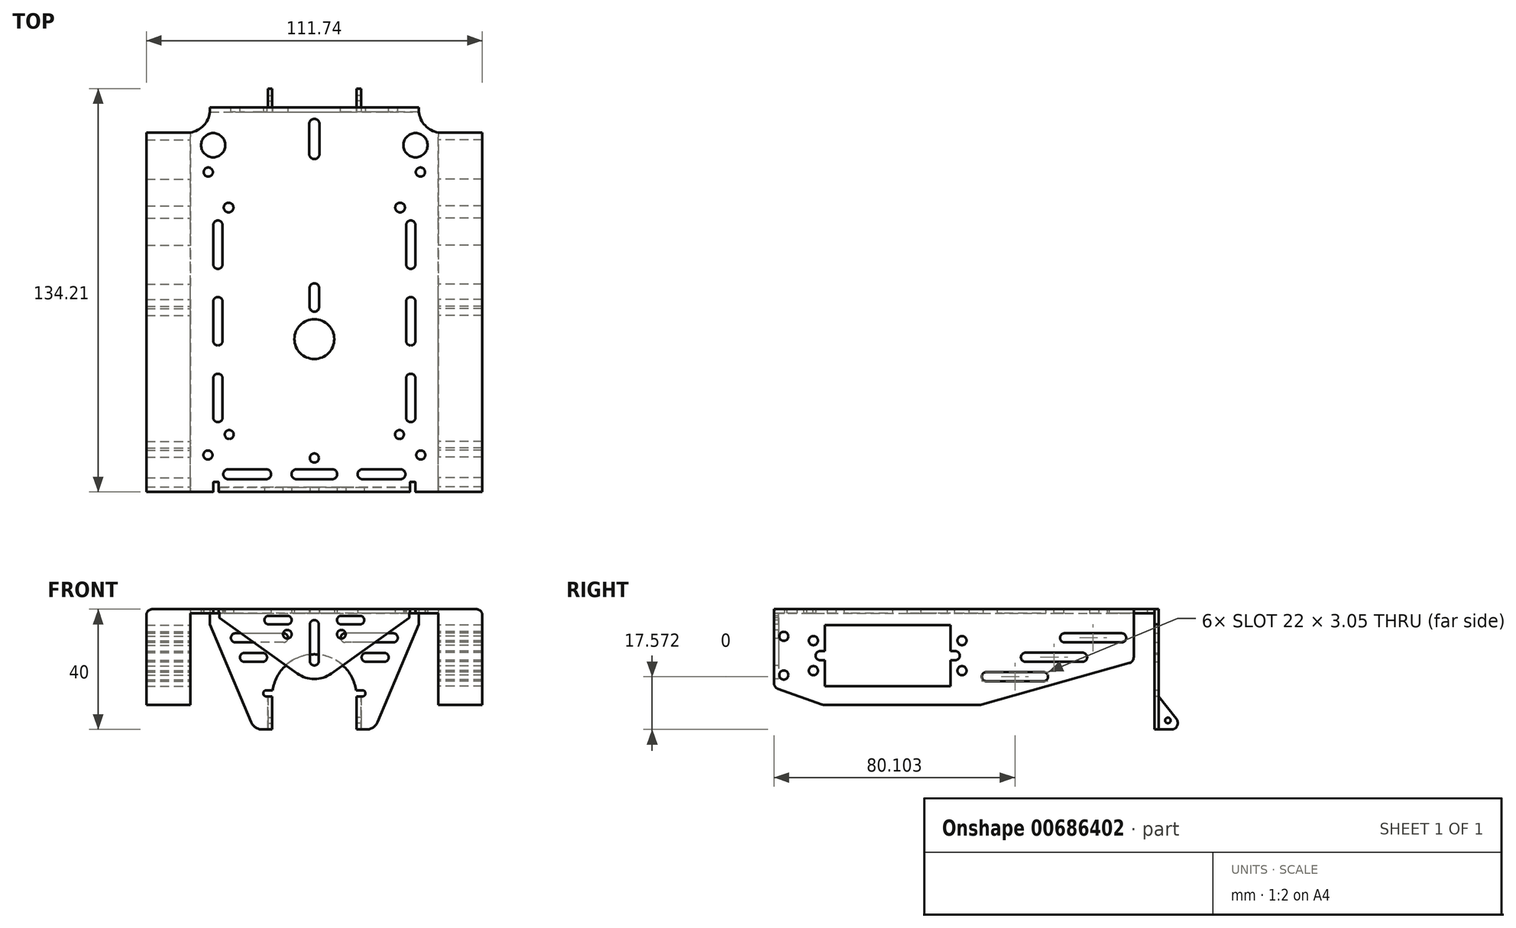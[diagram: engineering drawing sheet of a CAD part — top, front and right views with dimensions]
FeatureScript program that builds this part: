
annotation { "Feature Type Name" : "Feature", "Feature Type Description" : "" }
export const myFeature = defineFeature(function(context is Context, id is Id, definition is map)
    precondition{}
    {
        {
            var Q0;
            Q0=qCreatedBy(makeId("Top.planeOp"),FACE);
            var sketch = newSketch(context, id + "F0", { "sketchPlane" : qUnion([Q0])});
            skLineSegment(sketch, "E0", {"start": v(40.6, 10) * mm, "end": v(40.6, 161.38) * mm});
            skArc(sketch, "E1", {"start": v(40.6, 161.38) * mm, "mid": v(46.2, 164.32) * mm, "end": v(48.85, 170.09) * mm});
            skLineSegment(sketch, "E2", {"start": v(48.85, 170.09) * mm, "end": v(92.83, 170.09) * mm});
            skLineSegment(sketch, "E3", {"start": v(92.83, 170.09) * mm, "end": v(92.83, 10) * mm});
            skLineSegment(sketch, "E4", {"start": v(92.83, 10) * mm, "end": v(52.83, 10) * mm});
            skCircle(sketch, "E5", {"center": v(50.26, 156.03) * mm, "radius": 5.1 * mm});
            skCircle(sketch, "E6", {"center": v(48.18, 144.7) * mm, "radius": 1.93 * mm});
            skCircle(sketch, "E7", {"center": v(56.74, 129.77) * mm, "radius": 2.04 * mm});
            skCircle(sketch, "E8", {"center": v(57.01, 34.19) * mm, "radius": 1.88 * mm});
            skLineSegment(sketch, "E9.left", {"start": v(50.29, 122.36) * mm, "end": v(50.29, 105.92) * mm});
            skLineSegment(sketch, "E9.right", {"start": v(54.22, 122.36) * mm, "end": v(54.22, 105.92) * mm});
            skLineSegment(sketch, "E10.bottom", {"start": v(56.62, 19.58) * mm, "end": v(72.52, 19.58) * mm});
            skLineSegment(sketch, "E10.top", {"start": v(56.62, 15.38) * mm, "end": v(72.52, 15.38) * mm});
            skArc(sketch, "E11", {"start": v(50.29, 105.92) * mm, "mid": v(52.25, 103.95) * mm, "end": v(54.22, 105.92) * mm});
            skArc(sketch, "E12", {"start": v(54.22, 122.36) * mm, "mid": v(52.25, 124.33) * mm, "end": v(50.29, 122.36) * mm});
            skArc(sketch, "E13", {"start": v(56.62, 19.58) * mm, "mid": v(54.52, 17.48) * mm, "end": v(56.62, 15.38) * mm});
            skArc(sketch, "E14", {"start": v(72.52, 15.38) * mm, "mid": v(74.62, 17.48) * mm, "end": v(72.52, 19.58) * mm});
            skLineSegment(sketch, "E15.0.1.0", {"start": v(50.29, 90.1) * mm, "end": v(50.29, 73.66) * mm});
            skArc(sketch, "E15.0.1.1", {"start": v(54.22, 90.1) * mm, "mid": v(52.25, 92.07) * mm, "end": v(50.29, 90.1) * mm});
            skLineSegment(sketch, "E15.0.1.2", {"start": v(54.22, 90.1) * mm, "end": v(54.22, 73.66) * mm});
            skArc(sketch, "E15.0.1.3", {"start": v(50.29, 73.66) * mm, "mid": v(52.25, 71.7) * mm, "end": v(54.22, 73.66) * mm});
            skLineSegment(sketch, "E15.0.2.0", {"start": v(50.29, 57.84) * mm, "end": v(50.29, 41.4) * mm});
            skArc(sketch, "E15.0.2.1", {"start": v(54.22, 57.84) * mm, "mid": v(52.25, 59.8) * mm, "end": v(50.29, 57.84) * mm});
            skLineSegment(sketch, "E15.0.2.2", {"start": v(54.22, 57.84) * mm, "end": v(54.22, 41.4) * mm});
            skArc(sketch, "E15.0.2.3", {"start": v(50.29, 41.4) * mm, "mid": v(52.25, 39.43) * mm, "end": v(54.22, 41.4) * mm});
            skLineSegment(sketch, "E15.direction1", {"start": v(50.29, 105.92) * mm, "end": v(75.69, 105.92) * mm, "construction": true});
            skLineSegment(sketch, "E15.direction2", {"start": v(50.29, 105.92) * mm, "end": v(50.29, 73.66) * mm, "construction": true});
            skCircle(sketch, "E16", {"center": v(48.04, 25.57) * mm, "radius": 1.9 * mm});
            skArc(sketch, "E17", {"start": v(92.83, 82.78) * mm, "mid": v(84.45, 74.4) * mm, "end": v(92.83, 66.02) * mm});
            skArc(sketch, "E18", {"start": v(92.83, 26.24) * mm, "mid": v(90.9, 24.3) * mm, "end": v(92.83, 22.37) * mm});
            skLineSegment(sketch, "E19.left", {"start": v(90.68, 164.98) * mm, "end": v(90.68, 152.35) * mm});
            skArc(sketch, "E20", {"start": v(92.83, 167.14) * mm, "mid": v(91.3, 166.5) * mm, "end": v(90.68, 164.98) * mm});
            skArc(sketch, "E21", {"start": v(90.68, 152.35) * mm, "mid": v(91.3, 150.83) * mm, "end": v(92.83, 150.2) * mm});
            skLineSegment(sketch, "E22.left", {"start": v(90.82, 95.9) * mm, "end": v(90.82, 87.93) * mm});
            skArc(sketch, "E23", {"start": v(92.83, 97.9) * mm, "mid": v(91.4, 97.31) * mm, "end": v(90.82, 95.9) * mm});
            skArc(sketch, "E24", {"start": v(90.82, 87.93) * mm, "mid": v(91.4, 86.5) * mm, "end": v(92.83, 85.92) * mm});
            skLineSegment(sketch, "E25.1.0.0", {"start": v(85.32, 19.58) * mm, "end": v(92.83, 19.58) * mm});
            skArc(sketch, "E25.1.0.1", {"start": v(85.32, 19.58) * mm, "mid": v(83.22, 17.48) * mm, "end": v(85.32, 15.38) * mm});
            skLineSegment(sketch, "E25.1.0.2", {"start": v(85.32, 15.38) * mm, "end": v(92.83, 15.38) * mm});
            skLineSegment(sketch, "E25.direction1", {"start": v(56.62, 15.38) * mm, "end": v(85.32, 15.38) * mm, "construction": true});
            skPoint(sketch, "E26.orphan", {"position": v(101.22, 15.38) * mm});
            skArc(sketch, "E27.MirrorCS", {"start": v(135.38, 105.92) * mm, "mid": v(133.4, 103.95) * mm, "end": v(131.44, 105.92) * mm});
            skArc(sketch, "E28.MirrorCS", {"start": v(131.44, 90.1) * mm, "mid": v(133.4, 92.07) * mm, "end": v(135.38, 90.1) * mm});
            skArc(sketch, "E29.MirrorCS", {"start": v(100.34, 19.58) * mm, "mid": v(102.44, 17.48) * mm, "end": v(100.34, 15.38) * mm});
            skArc(sketch, "E30.MirrorCS", {"start": v(135.38, 41.4) * mm, "mid": v(133.4, 39.43) * mm, "end": v(131.44, 41.4) * mm});
            skArc(sketch, "E31.MirrorCS", {"start": v(113.14, 15.38) * mm, "mid": v(111.04, 17.48) * mm, "end": v(113.14, 19.58) * mm});
            skArc(sketch, "E32.MirrorCS", {"start": v(129.04, 19.58) * mm, "mid": v(131.14, 17.48) * mm, "end": v(129.04, 15.38) * mm});
            skArc(sketch, "E33.MirrorCS", {"start": v(94.84, 87.93) * mm, "mid": v(94.25, 86.5) * mm, "end": v(92.83, 85.92) * mm});
            skArc(sketch, "E34.MirrorCS", {"start": v(135.38, 73.66) * mm, "mid": v(133.4, 71.7) * mm, "end": v(131.44, 73.66) * mm});
            skArc(sketch, "E35.MirrorCS", {"start": v(145.06, 161.38) * mm, "mid": v(139.45, 164.32) * mm, "end": v(136.82, 170.09) * mm});
            skArc(sketch, "E36.MirrorCS", {"start": v(131.44, 57.84) * mm, "mid": v(133.4, 59.8) * mm, "end": v(135.38, 57.84) * mm});
            skArc(sketch, "E37.MirrorCS", {"start": v(131.44, 122.36) * mm, "mid": v(133.4, 124.33) * mm, "end": v(135.38, 122.36) * mm});
            skArc(sketch, "E38.MirrorCS", {"start": v(92.83, 97.9) * mm, "mid": v(94.25, 97.31) * mm, "end": v(94.84, 95.9) * mm});
            skLineSegment(sketch, "E39.MirrorCS", {"start": v(94.99, 164.98) * mm, "end": v(94.99, 152.35) * mm});
            skLineSegment(sketch, "E40.MirrorCS", {"start": v(94.84, 95.9) * mm, "end": v(94.84, 87.93) * mm});
            skLineSegment(sketch, "E41.MirrorCS", {"start": v(100.34, 19.58) * mm, "end": v(92.83, 19.58) * mm});
            skArc(sketch, "E42.MirrorCS", {"start": v(92.83, 167.14) * mm, "mid": v(94.35, 166.5) * mm, "end": v(94.99, 164.98) * mm});
            skArc(sketch, "E43.MirrorCS", {"start": v(94.99, 152.35) * mm, "mid": v(94.35, 150.83) * mm, "end": v(92.83, 150.2) * mm});
            skLineSegment(sketch, "E44.MirrorCS", {"start": v(100.34, 15.38) * mm, "end": v(92.83, 15.38) * mm});
            skArc(sketch, "E45.MirrorCS", {"start": v(92.83, 26.24) * mm, "mid": v(94.77, 24.3) * mm, "end": v(92.83, 22.37) * mm});
            skCircle(sketch, "E46.MirrorC", {"center": v(128.92, 129.77) * mm, "radius": 2.04 * mm});
            skCircle(sketch, "E47.MirrorC", {"center": v(137.62, 25.57) * mm, "radius": 1.9 * mm});
            skCircle(sketch, "E48.MirrorC", {"center": v(137.48, 144.7) * mm, "radius": 1.93 * mm});
            skCircle(sketch, "E49.MirrorC", {"center": v(128.65, 34.19) * mm, "radius": 1.88 * mm});
            skLineSegment(sketch, "E50.MirrorCS", {"start": v(129.04, 15.38) * mm, "end": v(100.34, 15.38) * mm, "construction": true});
            skPoint(sketch, "E51.MirrorP", {"position": v(84.44, 15.38) * mm});
            skCircle(sketch, "E52.MirrorC", {"center": v(135.4, 156.03) * mm, "radius": 5.1 * mm});
            skLineSegment(sketch, "E53.MirrorCS", {"start": v(135.38, 122.36) * mm, "end": v(135.38, 105.92) * mm});
            skLineSegment(sketch, "E54.MirrorCS", {"start": v(135.38, 57.84) * mm, "end": v(135.38, 41.4) * mm});
            skLineSegment(sketch, "E55.MirrorCS", {"start": v(92.83, 10) * mm, "end": v(132.84, 10) * mm});
            skLineSegment(sketch, "E56.MirrorCS", {"start": v(135.38, 105.92) * mm, "end": v(109.98, 105.92) * mm, "construction": true});
            skLineSegment(sketch, "E57.MirrorCS", {"start": v(135.38, 105.92) * mm, "end": v(135.38, 73.66) * mm, "construction": true});
            skLineSegment(sketch, "E58.MirrorCS", {"start": v(135.38, 90.1) * mm, "end": v(135.38, 73.66) * mm});
            skLineSegment(sketch, "E59.MirrorCS", {"start": v(129.04, 19.58) * mm, "end": v(113.14, 19.58) * mm});
            skLineSegment(sketch, "E60.MirrorCS", {"start": v(131.44, 57.84) * mm, "end": v(131.44, 41.4) * mm});
            skLineSegment(sketch, "E61.MirrorCS", {"start": v(129.04, 15.38) * mm, "end": v(113.14, 15.38) * mm});
            skLineSegment(sketch, "E62.MirrorCS", {"start": v(131.44, 122.36) * mm, "end": v(131.44, 105.92) * mm});
            skLineSegment(sketch, "E63.MirrorCS", {"start": v(145.06, 10) * mm, "end": v(145.06, 161.38) * mm});
            skLineSegment(sketch, "E64.MirrorCS", {"start": v(131.44, 90.1) * mm, "end": v(131.44, 73.66) * mm});
            skLineSegment(sketch, "E65.MirrorCS", {"start": v(136.82, 170.09) * mm, "end": v(92.83, 170.09) * mm});
            skArc(sketch, "E66.MirrorCS", {"start": v(92.83, 82.78) * mm, "mid": v(101.21, 74.4) * mm, "end": v(92.83, 66.02) * mm});
            skLineSegment(sketch, "E67", {"start": v(50.36, 10.25) * mm, "end": v(50.36, 14.04) * mm});
            skLineSegment(sketch, "E68", {"start": v(50.62, 14.3) * mm, "end": v(52.32, 14.3) * mm});
            skLineSegment(sketch, "E69", {"start": v(52.57, 14.04) * mm, "end": v(52.57, 10.25) * mm});
            skLineSegment(sketch, "E70.trimOffspring", {"start": v(50.1, 10) * mm, "end": v(40.6, 10) * mm});
            skPoint(sketch, "E71.visualSharp", {"position": v(50.36, 10) * mm});
            skArc(sketch, "E71.filletArc", {"start": v(50.1, 10) * mm, "mid": v(50.29, 10.07) * mm, "end": v(50.36, 10.25) * mm});
            skPoint(sketch, "E72.visualSharp", {"position": v(52.57, 10) * mm});
            skArc(sketch, "E72.filletArc", {"start": v(52.57, 10.25) * mm, "mid": v(52.65, 10.07) * mm, "end": v(52.83, 10) * mm});
            skPoint(sketch, "E73.visualSharp", {"position": v(50.36, 14.3) * mm});
            skArc(sketch, "E73.filletArc", {"start": v(50.62, 14.3) * mm, "mid": v(50.44, 14.22) * mm, "end": v(50.36, 14.04) * mm});
            skPoint(sketch, "E74.visualSharp", {"position": v(52.57, 14.3) * mm});
            skArc(sketch, "E74.filletArc", {"start": v(52.57, 14.04) * mm, "mid": v(52.5, 14.22) * mm, "end": v(52.32, 14.3) * mm});
            skArc(sketch, "E75.MirrorCS", {"start": v(133.09, 10.25) * mm, "mid": v(133.01, 10.07) * mm, "end": v(132.84, 10) * mm});
            skLineSegment(sketch, "E76.MirrorCS", {"start": v(133.09, 14.04) * mm, "end": v(133.09, 10.25) * mm});
            skArc(sketch, "E77.MirrorCS", {"start": v(133.09, 14.04) * mm, "mid": v(133.16, 14.22) * mm, "end": v(133.34, 14.3) * mm});
            skLineSegment(sketch, "E78.MirrorCS", {"start": v(135.3, 10.25) * mm, "end": v(135.3, 14.04) * mm});
            skLineSegment(sketch, "E79.MirrorCS", {"start": v(135.05, 14.3) * mm, "end": v(133.34, 14.3) * mm});
            skArc(sketch, "E80.MirrorCS", {"start": v(135.05, 14.3) * mm, "mid": v(135.23, 14.22) * mm, "end": v(135.3, 14.04) * mm});
            skArc(sketch, "E81.MirrorCS", {"start": v(135.55, 10) * mm, "mid": v(135.37, 10.07) * mm, "end": v(135.3, 10.25) * mm});
            skLineSegment(sketch, "E82.trimOffspring", {"start": v(135.55, 10) * mm, "end": v(145.06, 10) * mm});
            skSolve(sketch);
        }
        {
            var Q0;
            Q0 = qSketchRegion(id + "F0", true);
            extrude(context, id + "F1", {"entities" : qUnion([Q0]), "depth" : 1.65 * mm, "offsetDistance" : 25.4 * mm});
        }
        {
            var Q0;
            Q0=makeQuery(id+"F1.opExtrude","SWEPT_BODY",BODY,{"disambiguationData":[OSD([sQuery(id+"F0.wireOp",EDGE,"E0"),sQuery(id+"F0.wireOp",EDGE,"E1"),sQuery(id+"F0.wireOp",EDGE,"E2"),sQuery(id+"F0.wireOp",EDGE,"E4"),sQuery(id+"F0.wireOp",EDGE,"E5"),sQuery(id+"F0.wireOp",EDGE,"E6"),sQuery(id+"F0.wireOp",EDGE,"E7"),sQuery(id+"F0.wireOp",EDGE,"E8"),sQuery(id+"F0.wireOp",EDGE,"E9.left"),sQuery(id+"F0.wireOp",EDGE,"E9.right"),sQuery(id+"F0.wireOp",EDGE,"E10.bottom"),sQuery(id+"F0.wireOp",EDGE,"E10.top"),sQuery(id+"F0.wireOp",EDGE,"E11"),sQuery(id+"F0.wireOp",EDGE,"E12"),sQuery(id+"F0.wireOp",EDGE,"E13"),sQuery(id+"F0.wireOp",EDGE,"E14"),sQuery(id+"F0.wireOp",EDGE,"E15.0.1.0"),sQuery(id+"F0.wireOp",EDGE,"E15.0.1.1"),sQuery(id+"F0.wireOp",EDGE,"E15.0.1.2"),sQuery(id+"F0.wireOp",EDGE,"E15.0.1.3"),sQuery(id+"F0.wireOp",EDGE,"E15.0.2.0"),sQuery(id+"F0.wireOp",EDGE,"E15.0.2.1"),sQuery(id+"F0.wireOp",EDGE,"E15.0.2.2"),sQuery(id+"F0.wireOp",EDGE,"E15.0.2.3"),sQuery(id+"F0.wireOp",EDGE,"E16"),sQuery(id+"F0.wireOp",EDGE,"E17"),sQuery(id+"F0.wireOp",EDGE,"E18"),sQuery(id+"F0.wireOp",EDGE,"E19.left"),sQuery(id+"F0.wireOp",EDGE,"E20"),sQuery(id+"F0.wireOp",EDGE,"E21"),sQuery(id+"F0.wireOp",EDGE,"E22.left"),sQuery(id+"F0.wireOp",EDGE,"E23"),sQuery(id+"F0.wireOp",EDGE,"E24"),sQuery(id+"F0.wireOp",EDGE,"E25.1.0.0"),sQuery(id+"F0.wireOp",EDGE,"E25.1.0.1"),sQuery(id+"F0.wireOp",EDGE,"E25.1.0.2"),sQuery(id+"F0.wireOp",EDGE,"E27.MirrorCS"),sQuery(id+"F0.wireOp",EDGE,"E28.MirrorCS"),sQuery(id+"F0.wireOp",EDGE,"E29.MirrorCS"),sQuery(id+"F0.wireOp",EDGE,"E30.MirrorCS"),sQuery(id+"F0.wireOp",EDGE,"E31.MirrorCS"),sQuery(id+"F0.wireOp",EDGE,"E32.MirrorCS"),sQuery(id+"F0.wireOp",EDGE,"E33.MirrorCS"),sQuery(id+"F0.wireOp",EDGE,"E34.MirrorCS"),sQuery(id+"F0.wireOp",EDGE,"E35.MirrorCS"),sQuery(id+"F0.wireOp",EDGE,"E36.MirrorCS"),sQuery(id+"F0.wireOp",EDGE,"E37.MirrorCS"),sQuery(id+"F0.wireOp",EDGE,"E38.MirrorCS"),sQuery(id+"F0.wireOp",EDGE,"E39.MirrorCS"),sQuery(id+"F0.wireOp",EDGE,"E40.MirrorCS"),sQuery(id+"F0.wireOp",EDGE,"E41.MirrorCS"),sQuery(id+"F0.wireOp",EDGE,"E42.MirrorCS"),sQuery(id+"F0.wireOp",EDGE,"E43.MirrorCS"),sQuery(id+"F0.wireOp",EDGE,"E44.MirrorCS"),sQuery(id+"F0.wireOp",EDGE,"E45.MirrorCS"),sQuery(id+"F0.wireOp",EDGE,"E46.MirrorC"),sQuery(id+"F0.wireOp",EDGE,"E47.MirrorC"),sQuery(id+"F0.wireOp",EDGE,"E48.MirrorC"),sQuery(id+"F0.wireOp",EDGE,"E49.MirrorC"),sQuery(id+"F0.wireOp",EDGE,"E52.MirrorC"),sQuery(id+"F0.wireOp",EDGE,"E53.MirrorCS"),sQuery(id+"F0.wireOp",EDGE,"E54.MirrorCS"),sQuery(id+"F0.wireOp",EDGE,"E55.MirrorCS"),sQuery(id+"F0.wireOp",EDGE,"E58.MirrorCS"),sQuery(id+"F0.wireOp",EDGE,"E59.MirrorCS"),sQuery(id+"F0.wireOp",EDGE,"E60.MirrorCS"),sQuery(id+"F0.wireOp",EDGE,"E61.MirrorCS"),sQuery(id+"F0.wireOp",EDGE,"E62.MirrorCS"),sQuery(id+"F0.wireOp",EDGE,"E63.MirrorCS"),sQuery(id+"F0.wireOp",EDGE,"E64.MirrorCS"),sQuery(id+"F0.wireOp",EDGE,"E65.MirrorCS"),sQuery(id+"F0.wireOp",EDGE,"E66.MirrorCS")])]});
            var Q1;
            Q1=qCreatedBy(makeId("Origin.pointOp"),VERTEX);
            transform(context, id + "F2", {"entities" : qUnion([Q0]), "transformType" : TransformType.SCALE_UNIFORMLY, "scale" : .83151, "scalePoint" : qUnion([Q1]), "makeCopy" : false});
        }
        {
            var Q0;
            Q0=makeQuery(id+"F1.opExtrude","SWEPT_FACE",FACE,{"disambiguationData":[OSD([sQuery(id+"F0.wireOp",EDGE,"E4")])]});
            var sketch = newSketch(context, id + "F3", { "sketchPlane" : qUnion([Q0])});
            skLineSegment(sketch, "E83", {"start": v(43.93, -1.68) * mm, "end": v(43.93, 0) * mm});
            skLineSegment(sketch, "E84", {"start": v(110.45, 0) * mm, "end": v(110.45, -1.68) * mm});
            skLineSegment(sketch, "E85", {"start": v(43.93, 0) * mm, "end": v(110.45, 0) * mm});
            skLineSegment(sketch, "E86", {"start": v(43.93, -1.68) * mm, "end": v(71.3, -21.2) * mm});
            skLineSegment(sketch, "E87", {"start": v(83.09, -21.2) * mm, "end": v(110.45, -1.68) * mm});
            skLineSegment(sketch, "E88", {"start": v(77.19, -25.4) * mm, "end": v(77.19, 0) * mm, "construction": true});
            skPoint(sketch, "E89.visualSharp", {"position": v(77.19, -25.4) * mm});
            skArc(sketch, "E89.filletArc", {"start": v(71.3, -21.2) * mm, "mid": v(77.19, -23.08) * mm, "end": v(83.09, -21.2) * mm});
            skPoint(sketch, "E90", {"position": v(77.19, -23.08) * mm});
            skArc(sketch, "E91", {"start": v(78.74, -3.99) * mm, "mid": v(77.19, -2.44) * mm, "end": v(75.64, -3.99) * mm});
            skLineSegment(sketch, "E92", {"start": v(75.64, -3.99) * mm, "end": v(75.64, -10.37) * mm});
            skLineSegment(sketch, "E93", {"start": v(78.74, -3.99) * mm, "end": v(78.74, -10.37) * mm});
            skPoint(sketch, "E94", {"position": v(77.19, -2.44) * mm});
            skLineSegment(sketch, "E95", {"start": v(75.64, -10.37) * mm, "end": v(78.74, -10.37) * mm, "construction": true});
            skLineSegment(sketch, "E96.MirrorCS", {"start": v(78.74, -16.76) * mm, "end": v(78.74, -10.37) * mm});
            skLineSegment(sketch, "E97.MirrorCS", {"start": v(75.64, -16.76) * mm, "end": v(75.64, -10.37) * mm});
            skArc(sketch, "E98.MirrorCS", {"start": v(78.74, -16.76) * mm, "mid": v(77.19, -18.31) * mm, "end": v(75.64, -16.76) * mm});
            skArc(sketch, "E99", {"start": v(86.65, -0.91) * mm, "mid": v(85.13, -2.44) * mm, "end": v(86.65, -3.96) * mm});
            skLineSegment(sketch, "E100", {"start": v(86.65, -0.91) * mm, "end": v(89.89, -0.91) * mm});
            skLineSegment(sketch, "E101", {"start": v(86.65, -3.96) * mm, "end": v(89.89, -3.96) * mm});
            skLineSegment(sketch, "E102", {"start": v(86.65, -2.44) * mm, "end": v(85.13, -2.44) * mm, "construction": true});
            skPoint(sketch, "E103", {"position": v(85.13, -2.44) * mm});
            skLineSegment(sketch, "E104", {"start": v(89.89, -0.91) * mm, "end": v(89.89, -3.96) * mm, "construction": true});
            skLineSegment(sketch, "E105.MirrorCS", {"start": v(93.13, -0.91) * mm, "end": v(89.89, -0.91) * mm});
            skLineSegment(sketch, "E106.MirrorCS", {"start": v(93.13, -3.96) * mm, "end": v(89.89, -3.96) * mm});
            skArc(sketch, "E107.MirrorCS", {"start": v(93.13, -0.91) * mm, "mid": v(94.65, -2.44) * mm, "end": v(93.13, -3.96) * mm});
            skLineSegment(sketch, "E108.MirrorCS", {"start": v(67.73, -2.44) * mm, "end": v(69.25, -2.44) * mm, "construction": true});
            skLineSegment(sketch, "E109.MirrorCS", {"start": v(64.49, -0.91) * mm, "end": v(64.49, -3.96) * mm, "construction": true});
            skLineSegment(sketch, "E110.MirrorCS", {"start": v(67.73, -3.96) * mm, "end": v(64.49, -3.96) * mm});
            skLineSegment(sketch, "E111.MirrorCS", {"start": v(67.73, -0.91) * mm, "end": v(64.49, -0.91) * mm});
            skLineSegment(sketch, "E112.MirrorCS", {"start": v(61.25, -3.96) * mm, "end": v(64.49, -3.96) * mm});
            skArc(sketch, "E113.MirrorCS", {"start": v(67.73, -0.91) * mm, "mid": v(69.25, -2.44) * mm, "end": v(67.73, -3.96) * mm});
            skLineSegment(sketch, "E114.MirrorCS", {"start": v(61.25, -0.91) * mm, "end": v(64.49, -0.91) * mm});
            skArc(sketch, "E115.MirrorCS", {"start": v(61.25, -0.91) * mm, "mid": v(59.73, -2.44) * mm, "end": v(61.25, -3.96) * mm});
            skPoint(sketch, "E116.MirrorP", {"position": v(69.25, -2.44) * mm});
            skCircle(sketch, "E117", {"center": v(86.65, -7.4) * mm, "radius": 1.52 * mm});
            skCircle(sketch, "E118.MirrorC", {"center": v(67.73, -7.4) * mm, "radius": 1.52 * mm});
            skSolve(sketch);
        }
        {
            var Q0;
            Q0 = qSketchRegion(id + "F3", true);
            extrude(context, id + "F4", {"entities" : qUnion([Q0]), "operationType" : NewBodyOperationType.ADD, "oppositeDirection" : true, "depth" : 1.65 * mm, "offsetDistance" : 25.4 * mm});
        }
        {
            var Q0;
            Q0=makeQuery(id+"F1.opExtrude","CAP_EDGE",EDGE,{"disambiguationData":[OSD([sQuery(id+"F0.wireOp",EDGE,"E4"),sQuery(id+"F0.wireOp",EDGE,"E55.MirrorCS")])],"isStart":false});
            fillet(context, id + "F5", {"entities" : qUnion([Q0]), "radius" : 1.27 * mm, "allowEdgeOverflow" : false});
        }
        {
            var Q0;
            Q0=makeQuery(id+"F1.opExtrude","SWEPT_BODY",BODY,{"disambiguationData":[OSD([sQuery(id+"F0.wireOp",EDGE,"E0"),sQuery(id+"F0.wireOp",EDGE,"E1"),sQuery(id+"F0.wireOp",EDGE,"E2"),sQuery(id+"F0.wireOp",EDGE,"E4"),sQuery(id+"F0.wireOp",EDGE,"E5"),sQuery(id+"F0.wireOp",EDGE,"E6"),sQuery(id+"F0.wireOp",EDGE,"E7"),sQuery(id+"F0.wireOp",EDGE,"E8"),sQuery(id+"F0.wireOp",EDGE,"E9.left"),sQuery(id+"F0.wireOp",EDGE,"E9.right"),sQuery(id+"F0.wireOp",EDGE,"E10.bottom"),sQuery(id+"F0.wireOp",EDGE,"E10.top"),sQuery(id+"F0.wireOp",EDGE,"E11"),sQuery(id+"F0.wireOp",EDGE,"E12"),sQuery(id+"F0.wireOp",EDGE,"E13"),sQuery(id+"F0.wireOp",EDGE,"E14"),sQuery(id+"F0.wireOp",EDGE,"E15.0.1.0"),sQuery(id+"F0.wireOp",EDGE,"E15.0.1.1"),sQuery(id+"F0.wireOp",EDGE,"E15.0.1.2"),sQuery(id+"F0.wireOp",EDGE,"E15.0.1.3"),sQuery(id+"F0.wireOp",EDGE,"E15.0.2.0"),sQuery(id+"F0.wireOp",EDGE,"E15.0.2.1"),sQuery(id+"F0.wireOp",EDGE,"E15.0.2.2"),sQuery(id+"F0.wireOp",EDGE,"E15.0.2.3"),sQuery(id+"F0.wireOp",EDGE,"E16"),sQuery(id+"F0.wireOp",EDGE,"E17"),sQuery(id+"F0.wireOp",EDGE,"E18"),sQuery(id+"F0.wireOp",EDGE,"E19.left"),sQuery(id+"F0.wireOp",EDGE,"E20"),sQuery(id+"F0.wireOp",EDGE,"E21"),sQuery(id+"F0.wireOp",EDGE,"E22.left"),sQuery(id+"F0.wireOp",EDGE,"E23"),sQuery(id+"F0.wireOp",EDGE,"E24"),sQuery(id+"F0.wireOp",EDGE,"E25.1.0.0"),sQuery(id+"F0.wireOp",EDGE,"E25.1.0.1"),sQuery(id+"F0.wireOp",EDGE,"E25.1.0.2"),sQuery(id+"F0.wireOp",EDGE,"E27.MirrorCS"),sQuery(id+"F0.wireOp",EDGE,"E28.MirrorCS"),sQuery(id+"F0.wireOp",EDGE,"E29.MirrorCS"),sQuery(id+"F0.wireOp",EDGE,"E30.MirrorCS"),sQuery(id+"F0.wireOp",EDGE,"E31.MirrorCS"),sQuery(id+"F0.wireOp",EDGE,"E32.MirrorCS"),sQuery(id+"F0.wireOp",EDGE,"E33.MirrorCS"),sQuery(id+"F0.wireOp",EDGE,"E34.MirrorCS"),sQuery(id+"F0.wireOp",EDGE,"E35.MirrorCS"),sQuery(id+"F0.wireOp",EDGE,"E36.MirrorCS"),sQuery(id+"F0.wireOp",EDGE,"E37.MirrorCS"),sQuery(id+"F0.wireOp",EDGE,"E38.MirrorCS"),sQuery(id+"F0.wireOp",EDGE,"E39.MirrorCS"),sQuery(id+"F0.wireOp",EDGE,"E40.MirrorCS"),sQuery(id+"F0.wireOp",EDGE,"E41.MirrorCS"),sQuery(id+"F0.wireOp",EDGE,"E42.MirrorCS"),sQuery(id+"F0.wireOp",EDGE,"E43.MirrorCS"),sQuery(id+"F0.wireOp",EDGE,"E44.MirrorCS"),sQuery(id+"F0.wireOp",EDGE,"E45.MirrorCS"),sQuery(id+"F0.wireOp",EDGE,"E46.MirrorC"),sQuery(id+"F0.wireOp",EDGE,"E47.MirrorC"),sQuery(id+"F0.wireOp",EDGE,"E48.MirrorC"),sQuery(id+"F0.wireOp",EDGE,"E49.MirrorC"),sQuery(id+"F0.wireOp",EDGE,"E52.MirrorC"),sQuery(id+"F0.wireOp",EDGE,"E53.MirrorCS"),sQuery(id+"F0.wireOp",EDGE,"E54.MirrorCS"),sQuery(id+"F0.wireOp",EDGE,"E55.MirrorCS"),sQuery(id+"F0.wireOp",EDGE,"E58.MirrorCS"),sQuery(id+"F0.wireOp",EDGE,"E59.MirrorCS"),sQuery(id+"F0.wireOp",EDGE,"E60.MirrorCS"),sQuery(id+"F0.wireOp",EDGE,"E61.MirrorCS"),sQuery(id+"F0.wireOp",EDGE,"E62.MirrorCS"),sQuery(id+"F0.wireOp",EDGE,"E63.MirrorCS"),sQuery(id+"F0.wireOp",EDGE,"E64.MirrorCS"),sQuery(id+"F0.wireOp",EDGE,"E65.MirrorCS"),sQuery(id+"F0.wireOp",EDGE,"E66.MirrorCS"),sQuery(id+"F0.wireOp",EDGE,"E67"),sQuery(id+"F0.wireOp",EDGE,"E68"),sQuery(id+"F0.wireOp",EDGE,"E69"),sQuery(id+"F0.wireOp",EDGE,"E70.trimOffspring"),sQuery(id+"F0.wireOp",EDGE,"E71.filletArc"),sQuery(id+"F0.wireOp",EDGE,"E72.filletArc"),sQuery(id+"F0.wireOp",EDGE,"E73.filletArc"),sQuery(id+"F0.wireOp",EDGE,"E74.filletArc"),sQuery(id+"F0.wireOp",EDGE,"E75.MirrorCS"),sQuery(id+"F0.wireOp",EDGE,"E76.MirrorCS"),sQuery(id+"F0.wireOp",EDGE,"E77.MirrorCS"),sQuery(id+"F0.wireOp",EDGE,"E78.MirrorCS"),sQuery(id+"F0.wireOp",EDGE,"E79.MirrorCS"),sQuery(id+"F0.wireOp",EDGE,"E80.MirrorCS"),sQuery(id+"F0.wireOp",EDGE,"E81.MirrorCS"),sQuery(id+"F0.wireOp",EDGE,"E82.trimOffspring")])]});
            var Q1;
            Q1=qCreatedBy(makeId("Origin.pointOp"),VERTEX);
            transform(context, id + "F6", {"entities" : qUnion([Q0]), "transformType" : TransformType.SCALE_UNIFORMLY, "scale" : .95, "scalePoint" : qUnion([Q1]), "makeCopy" : false});
        }
        {
            var Q0;
            Q0=makeQuery(id+"F1.opExtrude","SWEPT_FACE",FACE,{"disambiguationData":[OSD([sQuery(id+"F0.wireOp",EDGE,"E0")])]});
            var sketch = newSketch(context, id + "F7", { "sketchPlane" : qUnion([Q0])});
            skLineSegment(sketch, "E119", {"start": v(-7.9, 1.3) * mm, "end": v(-7.9, -23.29) * mm});
            skLineSegment(sketch, "E120", {"start": v(-9.22, -25.17) * mm, "end": v(-23.83, -30.38) * mm});
            skLineSegment(sketch, "E121", {"start": v(-24.5, -30.5) * mm, "end": v(-76.4, -30.5) * mm});
            skLineSegment(sketch, "E122", {"start": v(-76.94, -30.42) * mm, "end": v(-126.02, -16.6) * mm});
            skLineSegment(sketch, "E123", {"start": v(-127.48, -14.68) * mm, "end": v(-127.48, 1.3) * mm});
            skPoint(sketch, "E124.visualSharp", {"position": v(-127.48, -16.2) * mm});
            skArc(sketch, "E124.filletArc", {"start": v(-127.48, -14.68) * mm, "mid": v(-127.07, -15.89) * mm, "end": v(-126.02, -16.6) * mm});
            skPoint(sketch, "E125.visualSharp", {"position": v(-76.68, -30.5) * mm});
            skArc(sketch, "E125.filletArc", {"start": v(-76.94, -30.42) * mm, "mid": v(-76.67, -30.48) * mm, "end": v(-76.4, -30.5) * mm});
            skPoint(sketch, "E126.visualSharp", {"position": v(-24.15, -30.5) * mm});
            skArc(sketch, "E126.filletArc", {"start": v(-24.5, -30.5) * mm, "mid": v(-24.16, -30.47) * mm, "end": v(-23.83, -30.38) * mm});
            skPoint(sketch, "E127.visualSharp", {"position": v(-7.9, -24.7) * mm});
            skArc(sketch, "E127.filletArc", {"start": v(-9.22, -25.17) * mm, "mid": v(-8.26, -24.44) * mm, "end": v(-7.9, -23.29) * mm});
            skLineSegment(sketch, "E128", {"start": v(-127.48, 1.3) * mm, "end": v(-7.9, 1.3) * mm});
            skLineSegment(sketch, "E129.bottom", {"start": v(-66.64, -4.02) * mm, "end": v(-24.74, -4.02) * mm});
            skLineSegment(sketch, "E129.top", {"start": v(-66.64, -24.27) * mm, "end": v(-24.74, -24.27) * mm});
            skLineSegment(sketch, "E129.left", {"start": v(-66.64, -4.02) * mm, "end": v(-66.64, -12.64) * mm});
            skLineSegment(sketch, "E129.right", {"start": v(-24.74, -4.02) * mm, "end": v(-24.74, -12.64) * mm});
            skLineSegment(sketch, "E130", {"start": v(-45.7, -4.02) * mm, "end": v(-45.7, -24.27) * mm, "construction": true});
            skArc(sketch, "E131", {"start": v(-68.14, -12.64) * mm, "mid": v(-69.64, -14.14) * mm, "end": v(-68.14, -15.64) * mm});
            skPoint(sketch, "E131.centerSnap0", {"position": v(-66.64, -14.14) * mm});
            skLineSegment(sketch, "E132", {"start": v(-68.14, -12.64) * mm, "end": v(-66.64, -12.64) * mm});
            skLineSegment(sketch, "E133", {"start": v(-68.14, -15.64) * mm, "end": v(-66.64, -15.64) * mm});
            skLineSegment(sketch, "E134.trimOffspring", {"start": v(-66.64, -15.64) * mm, "end": v(-66.64, -24.27) * mm});
            skArc(sketch, "E135.MirrorCS", {"start": v(-23.24, -12.64) * mm, "mid": v(-21.74, -14.14) * mm, "end": v(-23.24, -15.64) * mm});
            skPoint(sketch, "E136.MirrorP", {"position": v(-24.74, -14.14) * mm});
            skLineSegment(sketch, "E137.MirrorCS", {"start": v(-23.24, -15.64) * mm, "end": v(-24.74, -15.64) * mm});
            skLineSegment(sketch, "E138.MirrorCS", {"start": v(-23.24, -12.64) * mm, "end": v(-24.74, -12.64) * mm});
            skLineSegment(sketch, "E139.trimOffspring", {"start": v(-24.74, -15.64) * mm, "end": v(-24.74, -24.27) * mm});
            skLineSegment(sketch, "E140", {"start": v(-68.14, -14.14) * mm, "end": v(-23.24, -14.14) * mm, "construction": true});
            skCircle(sketch, "E141", {"center": v(-70.4, -9.14) * mm, "radius": 1.52 * mm});
            skCircle(sketch, "E142.0.1.0", {"center": v(-70.4, -19.14) * mm, "radius": 1.52 * mm});
            skCircle(sketch, "E142.1.0.0", {"center": v(-21, -9.14) * mm, "radius": 1.52 * mm});
            skCircle(sketch, "E142.1.1.0", {"center": v(-21, -19.14) * mm, "radius": 1.52 * mm});
            skLineSegment(sketch, "E142.direction1", {"start": v(-70.4, -9.14) * mm, "end": v(-21, -9.14) * mm, "construction": true});
            skLineSegment(sketch, "E142.direction2", {"start": v(-70.4, -9.14) * mm, "end": v(-70.4, -19.14) * mm, "construction": true});
            skCircle(sketch, "E143", {"center": v(-11.15, -7.72) * mm, "radius": 1.52 * mm});
            skCircle(sketch, "E144", {"center": v(-11.15, -20.57) * mm, "radius": 1.52 * mm});
            skLineSegment(sketch, "E145", {"start": v(-11.15, -7.72) * mm, "end": v(-11.15, -20.57) * mm, "construction": true});
            skPoint(sketch, "E146", {"position": v(-11.15, -14.14) * mm});
            skArc(sketch, "E147", {"start": v(-123.48, -6.7) * mm, "mid": v(-125, -8.22) * mm, "end": v(-123.48, -9.74) * mm});
            skLineSegment(sketch, "E148", {"start": v(-123.48, -6.7) * mm, "end": v(-114, -6.7) * mm});
            skLineSegment(sketch, "E149", {"start": v(-123.48, -9.74) * mm, "end": v(-114, -9.74) * mm});
            skLineSegment(sketch, "E150", {"start": v(-114, -9.74) * mm, "end": v(-114, -6.7) * mm, "construction": true});
            skLineSegment(sketch, "E151.MirrorCS", {"start": v(-104.53, -6.7) * mm, "end": v(-114, -6.7) * mm});
            skLineSegment(sketch, "E152.MirrorCS", {"start": v(-104.53, -9.74) * mm, "end": v(-114, -9.74) * mm});
            skArc(sketch, "E153.MirrorCS", {"start": v(-104.53, -6.7) * mm, "mid": v(-103, -8.22) * mm, "end": v(-104.53, -9.74) * mm});
            skLineSegment(sketch, "E154.direction1", {"start": v(-123.48, -9.74) * mm, "end": v(-117.53, -9.74) * mm, "construction": true});
            skLineSegment(sketch, "E154.direction2", {"start": v(-123.48, -9.74) * mm, "end": v(-123.48, -16.2) * mm, "construction": true});
            skPoint(sketch, "E155", {"position": v(-110.48, -14.67) * mm});
            skArc(sketch, "E156", {"start": v(-110.48, -13.15) * mm, "mid": v(-112, -14.67) * mm, "end": v(-110.48, -16.2) * mm});
            skLineSegment(sketch, "E157", {"start": v(-110.48, -13.15) * mm, "end": v(-101, -13.15) * mm});
            skLineSegment(sketch, "E158", {"start": v(-110.48, -16.2) * mm, "end": v(-101, -16.2) * mm});
            skLineSegment(sketch, "E159", {"start": v(-101, -16.2) * mm, "end": v(-101, -13.15) * mm, "construction": true});
            skLineSegment(sketch, "E160.MirrorCS", {"start": v(-91.53, -13.15) * mm, "end": v(-101, -13.15) * mm});
            skLineSegment(sketch, "E161.MirrorCS", {"start": v(-91.53, -16.2) * mm, "end": v(-101, -16.2) * mm});
            skArc(sketch, "E162.MirrorCS", {"start": v(-91.53, -13.15) * mm, "mid": v(-90, -14.67) * mm, "end": v(-91.53, -16.2) * mm});
            skLineSegment(sketch, "E163.direction1", {"start": v(-110.48, -16.2) * mm, "end": v(-104.53, -16.2) * mm, "construction": true});
            skPoint(sketch, "E164", {"position": v(-97.48, -21.12) * mm});
            skArc(sketch, "E165", {"start": v(-97.48, -19.6) * mm, "mid": v(-99, -21.12) * mm, "end": v(-97.48, -22.65) * mm});
            skLineSegment(sketch, "E166", {"start": v(-97.48, -19.6) * mm, "end": v(-88, -19.6) * mm});
            skLineSegment(sketch, "E167", {"start": v(-97.48, -22.65) * mm, "end": v(-88, -22.65) * mm});
            skLineSegment(sketch, "E168", {"start": v(-88, -22.65) * mm, "end": v(-88, -19.6) * mm, "construction": true});
            skLineSegment(sketch, "E169.MirrorCS", {"start": v(-78.53, -19.6) * mm, "end": v(-88, -19.6) * mm});
            skLineSegment(sketch, "E170.MirrorCS", {"start": v(-78.53, -22.65) * mm, "end": v(-88, -22.65) * mm});
            skArc(sketch, "E171.MirrorCS", {"start": v(-78.53, -19.6) * mm, "mid": v(-77, -21.12) * mm, "end": v(-78.53, -22.65) * mm});
            skSolve(sketch);
        }
        {
            var Q0;
            Q0 = qSketchRegion(id + "F7", true);
            extrude(context, id + "F8", {"entities" : qUnion([Q0]), "operationType" : NewBodyOperationType.ADD, "depth" : (.575 * 25.4) * mm, "offsetDistance" : 25 * mm});
        }
        {
            var Q0;
            Q0=makeQuery(id+"F1.opExtrude","CAP_EDGE",EDGE,{"disambiguationData":[OSD([sQuery(id+"F0.wireOp",EDGE,"E24"),sQuery(id+"F0.wireOp",EDGE,"E33.MirrorCS")])],"isStart":false});
            cPoint(context, id + "F9", {"entities" : qUnion([Q0]), "parameter" : 0.5});
        }
        {
            var Q0;
            Q0=makeQuery(id+"F1.opExtrude","SWEPT_BODY",BODY,{"disambiguationData":[OSD([sQuery(id+"F0.wireOp",EDGE,"E0"),sQuery(id+"F0.wireOp",EDGE,"E1"),sQuery(id+"F0.wireOp",EDGE,"E2"),sQuery(id+"F0.wireOp",EDGE,"E4"),sQuery(id+"F0.wireOp",EDGE,"E5"),sQuery(id+"F0.wireOp",EDGE,"E6"),sQuery(id+"F0.wireOp",EDGE,"E7"),sQuery(id+"F0.wireOp",EDGE,"E8"),sQuery(id+"F0.wireOp",EDGE,"E9.left"),sQuery(id+"F0.wireOp",EDGE,"E9.right"),sQuery(id+"F0.wireOp",EDGE,"E10.bottom"),sQuery(id+"F0.wireOp",EDGE,"E10.top"),sQuery(id+"F0.wireOp",EDGE,"E11"),sQuery(id+"F0.wireOp",EDGE,"E12"),sQuery(id+"F0.wireOp",EDGE,"E13"),sQuery(id+"F0.wireOp",EDGE,"E14"),sQuery(id+"F0.wireOp",EDGE,"E15.0.1.0"),sQuery(id+"F0.wireOp",EDGE,"E15.0.1.1"),sQuery(id+"F0.wireOp",EDGE,"E15.0.1.2"),sQuery(id+"F0.wireOp",EDGE,"E15.0.1.3"),sQuery(id+"F0.wireOp",EDGE,"E15.0.2.0"),sQuery(id+"F0.wireOp",EDGE,"E15.0.2.1"),sQuery(id+"F0.wireOp",EDGE,"E15.0.2.2"),sQuery(id+"F0.wireOp",EDGE,"E15.0.2.3"),sQuery(id+"F0.wireOp",EDGE,"E16"),sQuery(id+"F0.wireOp",EDGE,"E17"),sQuery(id+"F0.wireOp",EDGE,"E18"),sQuery(id+"F0.wireOp",EDGE,"E19.left"),sQuery(id+"F0.wireOp",EDGE,"E20"),sQuery(id+"F0.wireOp",EDGE,"E21"),sQuery(id+"F0.wireOp",EDGE,"E22.left"),sQuery(id+"F0.wireOp",EDGE,"E23"),sQuery(id+"F0.wireOp",EDGE,"E24"),sQuery(id+"F0.wireOp",EDGE,"E25.1.0.0"),sQuery(id+"F0.wireOp",EDGE,"E25.1.0.1"),sQuery(id+"F0.wireOp",EDGE,"E25.1.0.2"),sQuery(id+"F0.wireOp",EDGE,"E27.MirrorCS"),sQuery(id+"F0.wireOp",EDGE,"E28.MirrorCS"),sQuery(id+"F0.wireOp",EDGE,"E29.MirrorCS"),sQuery(id+"F0.wireOp",EDGE,"E30.MirrorCS"),sQuery(id+"F0.wireOp",EDGE,"E31.MirrorCS"),sQuery(id+"F0.wireOp",EDGE,"E32.MirrorCS"),sQuery(id+"F0.wireOp",EDGE,"E33.MirrorCS"),sQuery(id+"F0.wireOp",EDGE,"E34.MirrorCS"),sQuery(id+"F0.wireOp",EDGE,"E35.MirrorCS"),sQuery(id+"F0.wireOp",EDGE,"E36.MirrorCS"),sQuery(id+"F0.wireOp",EDGE,"E37.MirrorCS"),sQuery(id+"F0.wireOp",EDGE,"E38.MirrorCS"),sQuery(id+"F0.wireOp",EDGE,"E39.MirrorCS"),sQuery(id+"F0.wireOp",EDGE,"E40.MirrorCS"),sQuery(id+"F0.wireOp",EDGE,"E41.MirrorCS"),sQuery(id+"F0.wireOp",EDGE,"E42.MirrorCS"),sQuery(id+"F0.wireOp",EDGE,"E43.MirrorCS"),sQuery(id+"F0.wireOp",EDGE,"E44.MirrorCS"),sQuery(id+"F0.wireOp",EDGE,"E45.MirrorCS"),sQuery(id+"F0.wireOp",EDGE,"E46.MirrorC"),sQuery(id+"F0.wireOp",EDGE,"E47.MirrorC"),sQuery(id+"F0.wireOp",EDGE,"E48.MirrorC"),sQuery(id+"F0.wireOp",EDGE,"E49.MirrorC"),sQuery(id+"F0.wireOp",EDGE,"E52.MirrorC"),sQuery(id+"F0.wireOp",EDGE,"E53.MirrorCS"),sQuery(id+"F0.wireOp",EDGE,"E54.MirrorCS"),sQuery(id+"F0.wireOp",EDGE,"E55.MirrorCS"),sQuery(id+"F0.wireOp",EDGE,"E58.MirrorCS"),sQuery(id+"F0.wireOp",EDGE,"E59.MirrorCS"),sQuery(id+"F0.wireOp",EDGE,"E60.MirrorCS"),sQuery(id+"F0.wireOp",EDGE,"E61.MirrorCS"),sQuery(id+"F0.wireOp",EDGE,"E62.MirrorCS"),sQuery(id+"F0.wireOp",EDGE,"E63.MirrorCS"),sQuery(id+"F0.wireOp",EDGE,"E64.MirrorCS"),sQuery(id+"F0.wireOp",EDGE,"E65.MirrorCS"),sQuery(id+"F0.wireOp",EDGE,"E66.MirrorCS"),sQuery(id+"F0.wireOp",EDGE,"E67"),sQuery(id+"F0.wireOp",EDGE,"E68"),sQuery(id+"F0.wireOp",EDGE,"E69"),sQuery(id+"F0.wireOp",EDGE,"E70.trimOffspring"),sQuery(id+"F0.wireOp",EDGE,"E71.filletArc"),sQuery(id+"F0.wireOp",EDGE,"E72.filletArc"),sQuery(id+"F0.wireOp",EDGE,"E73.filletArc"),sQuery(id+"F0.wireOp",EDGE,"E74.filletArc"),sQuery(id+"F0.wireOp",EDGE,"E75.MirrorCS"),sQuery(id+"F0.wireOp",EDGE,"E76.MirrorCS"),sQuery(id+"F0.wireOp",EDGE,"E77.MirrorCS"),sQuery(id+"F0.wireOp",EDGE,"E78.MirrorCS"),sQuery(id+"F0.wireOp",EDGE,"E79.MirrorCS"),sQuery(id+"F0.wireOp",EDGE,"E80.MirrorCS"),sQuery(id+"F0.wireOp",EDGE,"E81.MirrorCS"),sQuery(id+"F0.wireOp",EDGE,"E82.trimOffspring")])]});
            var Q1;
            Q1 = qCreatedBy(id + "F9" ,VERTEX);
            var Q2;
            Q2=qCreatedBy(makeId("Origin.pointOp"),VERTEX);
            transform(context, id + "F10", {"entities" : qUnion([Q0]), "transformType" : TransformType.TRANSLATION_ENTITY, "oppositeDirectionEntity" : false, "transformLine" : qUnion([Q1, Q2]), "makeCopy" : false});
        }
        {
            var Q0;
            Q0=makeQuery(id+"F1.opExtrude","SWEPT_BODY",BODY,{"disambiguationData":[OSD([sQuery(id+"F0.wireOp",EDGE,"E0"),sQuery(id+"F0.wireOp",EDGE,"E1"),sQuery(id+"F0.wireOp",EDGE,"E2"),sQuery(id+"F0.wireOp",EDGE,"E4"),sQuery(id+"F0.wireOp",EDGE,"E5"),sQuery(id+"F0.wireOp",EDGE,"E6"),sQuery(id+"F0.wireOp",EDGE,"E7"),sQuery(id+"F0.wireOp",EDGE,"E8"),sQuery(id+"F0.wireOp",EDGE,"E9.left"),sQuery(id+"F0.wireOp",EDGE,"E9.right"),sQuery(id+"F0.wireOp",EDGE,"E10.bottom"),sQuery(id+"F0.wireOp",EDGE,"E10.top"),sQuery(id+"F0.wireOp",EDGE,"E11"),sQuery(id+"F0.wireOp",EDGE,"E12"),sQuery(id+"F0.wireOp",EDGE,"E13"),sQuery(id+"F0.wireOp",EDGE,"E14"),sQuery(id+"F0.wireOp",EDGE,"E15.0.1.0"),sQuery(id+"F0.wireOp",EDGE,"E15.0.1.1"),sQuery(id+"F0.wireOp",EDGE,"E15.0.1.2"),sQuery(id+"F0.wireOp",EDGE,"E15.0.1.3"),sQuery(id+"F0.wireOp",EDGE,"E15.0.2.0"),sQuery(id+"F0.wireOp",EDGE,"E15.0.2.1"),sQuery(id+"F0.wireOp",EDGE,"E15.0.2.2"),sQuery(id+"F0.wireOp",EDGE,"E15.0.2.3"),sQuery(id+"F0.wireOp",EDGE,"E16"),sQuery(id+"F0.wireOp",EDGE,"E17"),sQuery(id+"F0.wireOp",EDGE,"E18"),sQuery(id+"F0.wireOp",EDGE,"E19.left"),sQuery(id+"F0.wireOp",EDGE,"E20"),sQuery(id+"F0.wireOp",EDGE,"E21"),sQuery(id+"F0.wireOp",EDGE,"E22.left"),sQuery(id+"F0.wireOp",EDGE,"E23"),sQuery(id+"F0.wireOp",EDGE,"E24"),sQuery(id+"F0.wireOp",EDGE,"E25.1.0.0"),sQuery(id+"F0.wireOp",EDGE,"E25.1.0.1"),sQuery(id+"F0.wireOp",EDGE,"E25.1.0.2"),sQuery(id+"F0.wireOp",EDGE,"E27.MirrorCS"),sQuery(id+"F0.wireOp",EDGE,"E28.MirrorCS"),sQuery(id+"F0.wireOp",EDGE,"E29.MirrorCS"),sQuery(id+"F0.wireOp",EDGE,"E30.MirrorCS"),sQuery(id+"F0.wireOp",EDGE,"E31.MirrorCS"),sQuery(id+"F0.wireOp",EDGE,"E32.MirrorCS"),sQuery(id+"F0.wireOp",EDGE,"E33.MirrorCS"),sQuery(id+"F0.wireOp",EDGE,"E34.MirrorCS"),sQuery(id+"F0.wireOp",EDGE,"E35.MirrorCS"),sQuery(id+"F0.wireOp",EDGE,"E36.MirrorCS"),sQuery(id+"F0.wireOp",EDGE,"E37.MirrorCS"),sQuery(id+"F0.wireOp",EDGE,"E38.MirrorCS"),sQuery(id+"F0.wireOp",EDGE,"E39.MirrorCS"),sQuery(id+"F0.wireOp",EDGE,"E40.MirrorCS"),sQuery(id+"F0.wireOp",EDGE,"E41.MirrorCS"),sQuery(id+"F0.wireOp",EDGE,"E42.MirrorCS"),sQuery(id+"F0.wireOp",EDGE,"E43.MirrorCS"),sQuery(id+"F0.wireOp",EDGE,"E44.MirrorCS"),sQuery(id+"F0.wireOp",EDGE,"E45.MirrorCS"),sQuery(id+"F0.wireOp",EDGE,"E46.MirrorC"),sQuery(id+"F0.wireOp",EDGE,"E47.MirrorC"),sQuery(id+"F0.wireOp",EDGE,"E48.MirrorC"),sQuery(id+"F0.wireOp",EDGE,"E49.MirrorC"),sQuery(id+"F0.wireOp",EDGE,"E52.MirrorC"),sQuery(id+"F0.wireOp",EDGE,"E53.MirrorCS"),sQuery(id+"F0.wireOp",EDGE,"E54.MirrorCS"),sQuery(id+"F0.wireOp",EDGE,"E55.MirrorCS"),sQuery(id+"F0.wireOp",EDGE,"E58.MirrorCS"),sQuery(id+"F0.wireOp",EDGE,"E59.MirrorCS"),sQuery(id+"F0.wireOp",EDGE,"E60.MirrorCS"),sQuery(id+"F0.wireOp",EDGE,"E61.MirrorCS"),sQuery(id+"F0.wireOp",EDGE,"E62.MirrorCS"),sQuery(id+"F0.wireOp",EDGE,"E63.MirrorCS"),sQuery(id+"F0.wireOp",EDGE,"E64.MirrorCS"),sQuery(id+"F0.wireOp",EDGE,"E65.MirrorCS"),sQuery(id+"F0.wireOp",EDGE,"E66.MirrorCS"),sQuery(id+"F0.wireOp",EDGE,"E67"),sQuery(id+"F0.wireOp",EDGE,"E68"),sQuery(id+"F0.wireOp",EDGE,"E69"),sQuery(id+"F0.wireOp",EDGE,"E70.trimOffspring"),sQuery(id+"F0.wireOp",EDGE,"E71.filletArc"),sQuery(id+"F0.wireOp",EDGE,"E72.filletArc"),sQuery(id+"F0.wireOp",EDGE,"E73.filletArc"),sQuery(id+"F0.wireOp",EDGE,"E74.filletArc"),sQuery(id+"F0.wireOp",EDGE,"E75.MirrorCS"),sQuery(id+"F0.wireOp",EDGE,"E76.MirrorCS"),sQuery(id+"F0.wireOp",EDGE,"E77.MirrorCS"),sQuery(id+"F0.wireOp",EDGE,"E78.MirrorCS"),sQuery(id+"F0.wireOp",EDGE,"E79.MirrorCS"),sQuery(id+"F0.wireOp",EDGE,"E80.MirrorCS"),sQuery(id+"F0.wireOp",EDGE,"E81.MirrorCS"),sQuery(id+"F0.wireOp",EDGE,"E82.trimOffspring")])]});
            var Q1;
            Q1=qCreatedBy(makeId("Right.planeOp"),FACE);
            mirror(context, id + "F11", {"operationType" : NewBodyOperationType.ADD, "entities" : qUnion([Q0]), "mirrorPlane" : qUnion([Q1])});
        }
        {
            var Q0;
            Q0=makeQuery(id+"F8.opExtrude","CAP_EDGE",EDGE,{"disambiguationData":[OSD([sQuery(id+"F7.wireOp",EDGE,"E128")])],"isStart":false});
            var Q1;
            Q1=makeQuery(id+"F11.opPattern","COPY",EDGE,{"derivedFrom":makeQuery(id+"F8.opExtrude","CAP_EDGE",EDGE,{"disambiguationData":[OSD([sQuery(id+"F7.wireOp",EDGE,"E128")])],"isStart":false}),"instanceName":"1"});
            fillet(context, id + "F12", {"entities" : qUnion([Q0, Q1]), "radius" : 2 * mm, "tangentPropagation" : true, "allowEdgeOverflow" : false});
        }
        {
            var Q0;
            Q0=makeQuery(id+"F1.opExtrude","SWEPT_FACE",FACE,{"disambiguationData":[OSD([sQuery(id+"F0.wireOp",EDGE,"E2"),sQuery(id+"F0.wireOp",EDGE,"E65.MirrorCS")])]});
            var sketch = newSketch(context, id + "F13", { "sketchPlane" : qUnion([Q0])});
            skLineSegment(sketch, "E172", {"start": v(-34.75, 0) * mm, "end": v(-34.75, -5) * mm});
            skLineSegment(sketch, "E173", {"start": v(-34.75, -5) * mm, "end": v(-21.03, -37.55) * mm});
            skLineSegment(sketch, "E174", {"start": v(-20, -40) * mm, "end": v(0, -40) * mm, "construction": true});
            skLineSegment(sketch, "E175", {"start": v(-14, -40) * mm, "end": v(-14, -29) * mm});
            skArc(sketch, "E176", {"start": v(0, -15) * mm, "mid": v(-9.17, -18.42) * mm, "end": v(-13.86, -27) * mm});
            skPoint(sketch, "E177", {"position": v(-14, -29) * mm});
            skLineSegment(sketch, "E178", {"start": v(-14, -29) * mm, "end": v(0, -29) * mm, "construction": true});
            skLineSegment(sketch, "E179", {"start": v(0, -29) * mm, "end": v(0, -15) * mm, "construction": true});
            skLineSegment(sketch, "E180", {"start": v(-17.34, -40) * mm, "end": v(-14, -40) * mm});
            skLineSegment(sketch, "E181.MirrorCS", {"start": v(17.34, -40) * mm, "end": v(14, -40) * mm});
            skLineSegment(sketch, "E182.MirrorCS", {"start": v(14, -29) * mm, "end": v(0, -29) * mm, "construction": true});
            skArc(sketch, "E183.MirrorCS", {"start": v(0, -15) * mm, "mid": v(9.17, -18.42) * mm, "end": v(13.86, -27) * mm});
            skLineSegment(sketch, "E184.MirrorCS", {"start": v(14, -40) * mm, "end": v(14, -29) * mm});
            skLineSegment(sketch, "E185.MirrorCS", {"start": v(20, -40) * mm, "end": v(0, -40) * mm, "construction": true});
            skPoint(sketch, "E186.MirrorP", {"position": v(14, -29) * mm});
            skLineSegment(sketch, "E187.MirrorCS", {"start": v(34.75, 0) * mm, "end": v(34.75, -5) * mm});
            skLineSegment(sketch, "E188.MirrorCS", {"start": v(34.75, -5) * mm, "end": v(21.03, -37.55) * mm});
            skLineSegment(sketch, "E189", {"start": v(-34.75, 0) * mm, "end": v(34.75, 0) * mm});
            skArc(sketch, "E190", {"start": v(-16, -27) * mm, "mid": v(-17, -28) * mm, "end": v(-16, -29) * mm});
            skLineSegment(sketch, "E191", {"start": v(-16, -27) * mm, "end": v(-14, -27) * mm});
            skLineSegment(sketch, "E192", {"start": v(-16, -29) * mm, "end": v(-14, -29) * mm});
            skLineSegment(sketch, "E193", {"start": v(-14, -27) * mm, "end": v(-13.86, -27) * mm});
            skArc(sketch, "E194.MirrorCS", {"start": v(16, -27) * mm, "mid": v(17, -28) * mm, "end": v(16, -29) * mm});
            skLineSegment(sketch, "E195.MirrorCS", {"start": v(16, -29) * mm, "end": v(14, -29) * mm});
            skLineSegment(sketch, "E196.MirrorCS", {"start": v(16, -27) * mm, "end": v(14, -27) * mm});
            skLineSegment(sketch, "E197.MirrorCS", {"start": v(14, -27) * mm, "end": v(13.86, -27) * mm});
            skPoint(sketch, "E198.orphan", {"position": v(14, -27) * mm});
            skPoint(sketch, "E199.visualSharp", {"position": v(-20, -40) * mm});
            skArc(sketch, "E199.filletArc", {"start": v(-21.03, -37.55) * mm, "mid": v(-19.56, -39.33) * mm, "end": v(-17.34, -40) * mm});
            skPoint(sketch, "E200.visualSharp", {"position": v(20, -40) * mm});
            skArc(sketch, "E200.filletArc", {"start": v(17.34, -40) * mm, "mid": v(19.56, -39.33) * mm, "end": v(21.03, -37.55) * mm});
            skSolve(sketch);
        }
        {
            var Q0;
            Q0 = qSketchRegion(id + "F13", true);
            extrude(context, id + "F14", {"entities" : qUnion([Q0]), "operationType" : NewBodyOperationType.ADD, "depth" : 1.5 * mm, "offsetDistance" : 25 * mm});
        }
        {
            var Q0;
            Q0=makeQuery(id+"F14.opExtrude","CAP_FACE",FACE,{"disambiguationData":[OSD([sQuery(id+"F13.wireOp",EDGE,"E172"),sQuery(id+"F13.wireOp",EDGE,"E173"),sQuery(id+"F13.wireOp",EDGE,"E175"),sQuery(id+"F13.wireOp",EDGE,"E176"),sQuery(id+"F13.wireOp",EDGE,"E180"),sQuery(id+"F13.wireOp",EDGE,"E181.MirrorCS"),sQuery(id+"F13.wireOp",EDGE,"E183.MirrorCS"),sQuery(id+"F13.wireOp",EDGE,"E184.MirrorCS"),sQuery(id+"F13.wireOp",EDGE,"E187.MirrorCS"),sQuery(id+"F13.wireOp",EDGE,"E188.MirrorCS"),sQuery(id+"F13.wireOp",EDGE,"E189"),sQuery(id+"F13.wireOp",EDGE,"E190"),sQuery(id+"F13.wireOp",EDGE,"E191"),sQuery(id+"F13.wireOp",EDGE,"E192"),sQuery(id+"F13.wireOp",EDGE,"E193"),sQuery(id+"F13.wireOp",EDGE,"E194.MirrorCS"),sQuery(id+"F13.wireOp",EDGE,"E195.MirrorCS"),sQuery(id+"F13.wireOp",EDGE,"E196.MirrorCS"),sQuery(id+"F13.wireOp",EDGE,"E197.MirrorCS"),sQuery(id+"F13.wireOp",EDGE,"E199.filletArc"),sQuery(id+"F13.wireOp",EDGE,"E200.filletArc")])],"isStart":false});
            var sketch = newSketch(context, id + "F15", { "sketchPlane" : qUnion([Q0])});
            skArc(sketch, "E201", {"start": v(-26.22, -8) * mm, "mid": v(-27.75, -9.52) * mm, "end": v(-26.22, -11.05) * mm});
            skLineSegment(sketch, "E202", {"start": v(-26.22, -8) * mm, "end": v(-18.25, -8) * mm});
            skLineSegment(sketch, "E203", {"start": v(-26.22, -11.05) * mm, "end": v(-18.25, -11.05) * mm});
            skLineSegment(sketch, "E204", {"start": v(-18.25, -8) * mm, "end": v(-18.25, -11.05) * mm, "construction": true});
            skLineSegment(sketch, "E205.MirrorCS", {"start": v(-10.27, -8) * mm, "end": v(-18.25, -8) * mm});
            skLineSegment(sketch, "E206.MirrorCS", {"start": v(-10.27, -11.05) * mm, "end": v(-18.25, -11.05) * mm});
            skArc(sketch, "E207.MirrorCS", {"start": v(-10.27, -8) * mm, "mid": v(-8.75, -9.52) * mm, "end": v(-10.27, -11.05) * mm});
            skLineSegment(sketch, "E208", {"start": v(-26.22, -9.52) * mm, "end": v(-26.22, -8) * mm, "construction": true});
            skLineSegment(sketch, "E209", {"start": v(-23.22, -16.02) * mm, "end": v(-17.22, -16.02) * mm});
            skArc(sketch, "E210.0.startCap", {"start": v(-23.22, -17.52) * mm, "mid": v(-24.72, -16.02) * mm, "end": v(-23.22, -14.52) * mm});
            skArc(sketch, "E210.0.endCap", {"start": v(-17.22, -14.52) * mm, "mid": v(-15.72, -16.02) * mm, "end": v(-17.22, -17.52) * mm});
            skLineSegment(sketch, "E210.0.left", {"start": v(-23.22, -14.52) * mm, "end": v(-17.22, -14.52) * mm});
            skLineSegment(sketch, "E210.0.right", {"start": v(-23.22, -17.52) * mm, "end": v(-17.22, -17.52) * mm});
            skLineSegment(sketch, "E211.MirrorCS", {"start": v(23.22, -17.52) * mm, "end": v(17.22, -17.52) * mm});
            skLineSegment(sketch, "E212.MirrorCS", {"start": v(23.22, -14.52) * mm, "end": v(17.22, -14.52) * mm});
            skArc(sketch, "E213.MirrorCS", {"start": v(17.22, -14.52) * mm, "mid": v(15.72, -16.02) * mm, "end": v(17.22, -17.52) * mm});
            skArc(sketch, "E214.MirrorCS", {"start": v(23.22, -17.52) * mm, "mid": v(24.72, -16.02) * mm, "end": v(23.22, -14.52) * mm});
            skLineSegment(sketch, "E215.MirrorCS", {"start": v(26.22, -11.05) * mm, "end": v(18.25, -11.05) * mm});
            skLineSegment(sketch, "E216.MirrorCS", {"start": v(10.27, -8) * mm, "end": v(18.25, -8) * mm});
            skLineSegment(sketch, "E217.MirrorCS", {"start": v(10.27, -11.05) * mm, "end": v(18.25, -11.05) * mm});
            skLineSegment(sketch, "E218.MirrorCS", {"start": v(26.22, -9.52) * mm, "end": v(26.22, -8) * mm, "construction": true});
            skLineSegment(sketch, "E219.MirrorCS", {"start": v(18.25, -8) * mm, "end": v(18.25, -11.05) * mm, "construction": true});
            skArc(sketch, "E220.MirrorCS", {"start": v(10.27, -8) * mm, "mid": v(8.75, -9.52) * mm, "end": v(10.27, -11.05) * mm});
            skLineSegment(sketch, "E221.MirrorCS", {"start": v(23.22, -16.02) * mm, "end": v(17.22, -16.02) * mm});
            skLineSegment(sketch, "E222.MirrorCS", {"start": v(26.22, -8) * mm, "end": v(18.25, -8) * mm});
            skArc(sketch, "E223.MirrorCS", {"start": v(26.22, -8) * mm, "mid": v(27.75, -9.52) * mm, "end": v(26.22, -11.05) * mm});
            skSolve(sketch);
        }
        {
            var Q0;
            Q0 = qSketchRegion(id + "F15", true);
            extrude(context, id + "F16", {"entities" : qUnion([Q0]), "operationType" : NewBodyOperationType.REMOVE, "oppositeDirection" : true, "depth" : 25 * mm, "offsetDistance" : 25 * mm});
        }
        {
            var Q0;
            Q0=makeQuery(id+"F14.opExtrude","SWEPT_FACE",FACE,{"disambiguationData":[OSD([sQuery(id+"F13.wireOp",EDGE,"E175")])]});
            var sketch = newSketch(context, id + "F17", { "sketchPlane" : qUnion([Q0])});
            skLineSegment(sketch, "E224", {"start": v(-67.99, -29) * mm, "end": v(-73.81, -36.46) * mm});
            skLineSegment(sketch, "E225", {"start": v(-71.09, -40) * mm, "end": v(-66.49, -40) * mm});
            skLineSegment(sketch, "E226", {"start": v(-66.49, -40) * mm, "end": v(-66.49, -29) * mm});
            skLineSegment(sketch, "E227", {"start": v(-66.49, -29) * mm, "end": v(-67.99, -29) * mm});
            skCircle(sketch, "E228", {"center": v(-70.99, -37) * mm, "radius": 0.93 * mm});
            skLineSegment(sketch, "E229", {"start": v(-74.24, -37.69) * mm, "end": v(-74.24, -38) * mm});
            skLineSegment(sketch, "E230", {"start": v(-72.24, -40) * mm, "end": v(-71.09, -40) * mm});
            skPoint(sketch, "E231.visualSharp", {"position": v(-74.24, -37) * mm});
            skArc(sketch, "E231.filletArc", {"start": v(-73.81, -36.46) * mm, "mid": v(-74.13, -37.04) * mm, "end": v(-74.24, -37.69) * mm});
            skPoint(sketch, "E232.visualSharp", {"position": v(-74.24, -40) * mm});
            skArc(sketch, "E232.filletArc", {"start": v(-74.24, -38) * mm, "mid": v(-73.65, -39.41) * mm, "end": v(-72.24, -40) * mm});
            skSolve(sketch);
        }
        {
            var Q0;
            Q0 = qSketchRegion(id + "F17", true);
            extrude(context, id + "F18", {"entities" : qUnion([Q0]), "operationType" : NewBodyOperationType.ADD, "oppositeDirection" : true, "depth" : 1.5 * mm, "offsetDistance" : 25 * mm});
        }
        {
            var Q0;
            Q0=makeQuery(id+"F1.opExtrude","SWEPT_BODY",BODY,{"disambiguationData":[OSD([sQuery(id+"F0.wireOp",EDGE,"E0"),sQuery(id+"F0.wireOp",EDGE,"E1"),sQuery(id+"F0.wireOp",EDGE,"E2"),sQuery(id+"F0.wireOp",EDGE,"E4"),sQuery(id+"F0.wireOp",EDGE,"E5"),sQuery(id+"F0.wireOp",EDGE,"E6"),sQuery(id+"F0.wireOp",EDGE,"E7"),sQuery(id+"F0.wireOp",EDGE,"E8"),sQuery(id+"F0.wireOp",EDGE,"E9.left"),sQuery(id+"F0.wireOp",EDGE,"E9.right"),sQuery(id+"F0.wireOp",EDGE,"E10.bottom"),sQuery(id+"F0.wireOp",EDGE,"E10.top"),sQuery(id+"F0.wireOp",EDGE,"E11"),sQuery(id+"F0.wireOp",EDGE,"E12"),sQuery(id+"F0.wireOp",EDGE,"E13"),sQuery(id+"F0.wireOp",EDGE,"E14"),sQuery(id+"F0.wireOp",EDGE,"E15.0.1.0"),sQuery(id+"F0.wireOp",EDGE,"E15.0.1.1"),sQuery(id+"F0.wireOp",EDGE,"E15.0.1.2"),sQuery(id+"F0.wireOp",EDGE,"E15.0.1.3"),sQuery(id+"F0.wireOp",EDGE,"E15.0.2.0"),sQuery(id+"F0.wireOp",EDGE,"E15.0.2.1"),sQuery(id+"F0.wireOp",EDGE,"E15.0.2.2"),sQuery(id+"F0.wireOp",EDGE,"E15.0.2.3"),sQuery(id+"F0.wireOp",EDGE,"E16"),sQuery(id+"F0.wireOp",EDGE,"E17"),sQuery(id+"F0.wireOp",EDGE,"E18"),sQuery(id+"F0.wireOp",EDGE,"E19.left"),sQuery(id+"F0.wireOp",EDGE,"E20"),sQuery(id+"F0.wireOp",EDGE,"E21"),sQuery(id+"F0.wireOp",EDGE,"E22.left"),sQuery(id+"F0.wireOp",EDGE,"E23"),sQuery(id+"F0.wireOp",EDGE,"E24"),sQuery(id+"F0.wireOp",EDGE,"E25.1.0.0"),sQuery(id+"F0.wireOp",EDGE,"E25.1.0.1"),sQuery(id+"F0.wireOp",EDGE,"E25.1.0.2"),sQuery(id+"F0.wireOp",EDGE,"E27.MirrorCS"),sQuery(id+"F0.wireOp",EDGE,"E28.MirrorCS"),sQuery(id+"F0.wireOp",EDGE,"E29.MirrorCS"),sQuery(id+"F0.wireOp",EDGE,"E30.MirrorCS"),sQuery(id+"F0.wireOp",EDGE,"E31.MirrorCS"),sQuery(id+"F0.wireOp",EDGE,"E32.MirrorCS"),sQuery(id+"F0.wireOp",EDGE,"E33.MirrorCS"),sQuery(id+"F0.wireOp",EDGE,"E34.MirrorCS"),sQuery(id+"F0.wireOp",EDGE,"E35.MirrorCS"),sQuery(id+"F0.wireOp",EDGE,"E36.MirrorCS"),sQuery(id+"F0.wireOp",EDGE,"E37.MirrorCS"),sQuery(id+"F0.wireOp",EDGE,"E38.MirrorCS"),sQuery(id+"F0.wireOp",EDGE,"E39.MirrorCS"),sQuery(id+"F0.wireOp",EDGE,"E40.MirrorCS"),sQuery(id+"F0.wireOp",EDGE,"E41.MirrorCS"),sQuery(id+"F0.wireOp",EDGE,"E42.MirrorCS"),sQuery(id+"F0.wireOp",EDGE,"E43.MirrorCS"),sQuery(id+"F0.wireOp",EDGE,"E44.MirrorCS"),sQuery(id+"F0.wireOp",EDGE,"E45.MirrorCS"),sQuery(id+"F0.wireOp",EDGE,"E46.MirrorC"),sQuery(id+"F0.wireOp",EDGE,"E47.MirrorC"),sQuery(id+"F0.wireOp",EDGE,"E48.MirrorC"),sQuery(id+"F0.wireOp",EDGE,"E49.MirrorC"),sQuery(id+"F0.wireOp",EDGE,"E52.MirrorC"),sQuery(id+"F0.wireOp",EDGE,"E53.MirrorCS"),sQuery(id+"F0.wireOp",EDGE,"E54.MirrorCS"),sQuery(id+"F0.wireOp",EDGE,"E55.MirrorCS"),sQuery(id+"F0.wireOp",EDGE,"E58.MirrorCS"),sQuery(id+"F0.wireOp",EDGE,"E59.MirrorCS"),sQuery(id+"F0.wireOp",EDGE,"E60.MirrorCS"),sQuery(id+"F0.wireOp",EDGE,"E61.MirrorCS"),sQuery(id+"F0.wireOp",EDGE,"E62.MirrorCS"),sQuery(id+"F0.wireOp",EDGE,"E63.MirrorCS"),sQuery(id+"F0.wireOp",EDGE,"E64.MirrorCS"),sQuery(id+"F0.wireOp",EDGE,"E65.MirrorCS"),sQuery(id+"F0.wireOp",EDGE,"E66.MirrorCS"),sQuery(id+"F0.wireOp",EDGE,"E67"),sQuery(id+"F0.wireOp",EDGE,"E68"),sQuery(id+"F0.wireOp",EDGE,"E69"),sQuery(id+"F0.wireOp",EDGE,"E70.trimOffspring"),sQuery(id+"F0.wireOp",EDGE,"E71.filletArc"),sQuery(id+"F0.wireOp",EDGE,"E72.filletArc"),sQuery(id+"F0.wireOp",EDGE,"E73.filletArc"),sQuery(id+"F0.wireOp",EDGE,"E74.filletArc"),sQuery(id+"F0.wireOp",EDGE,"E75.MirrorCS"),sQuery(id+"F0.wireOp",EDGE,"E76.MirrorCS"),sQuery(id+"F0.wireOp",EDGE,"E77.MirrorCS"),sQuery(id+"F0.wireOp",EDGE,"E78.MirrorCS"),sQuery(id+"F0.wireOp",EDGE,"E79.MirrorCS"),sQuery(id+"F0.wireOp",EDGE,"E80.MirrorCS"),sQuery(id+"F0.wireOp",EDGE,"E81.MirrorCS"),sQuery(id+"F0.wireOp",EDGE,"E82.trimOffspring")])]});
            var Q1;
            Q1=qCreatedBy(makeId("Right.planeOp"),FACE);
            mirror(context, id + "F19", {"operationType" : NewBodyOperationType.ADD, "entities" : qUnion([Q0]), "mirrorPlane" : qUnion([Q1])});
        }
    });
